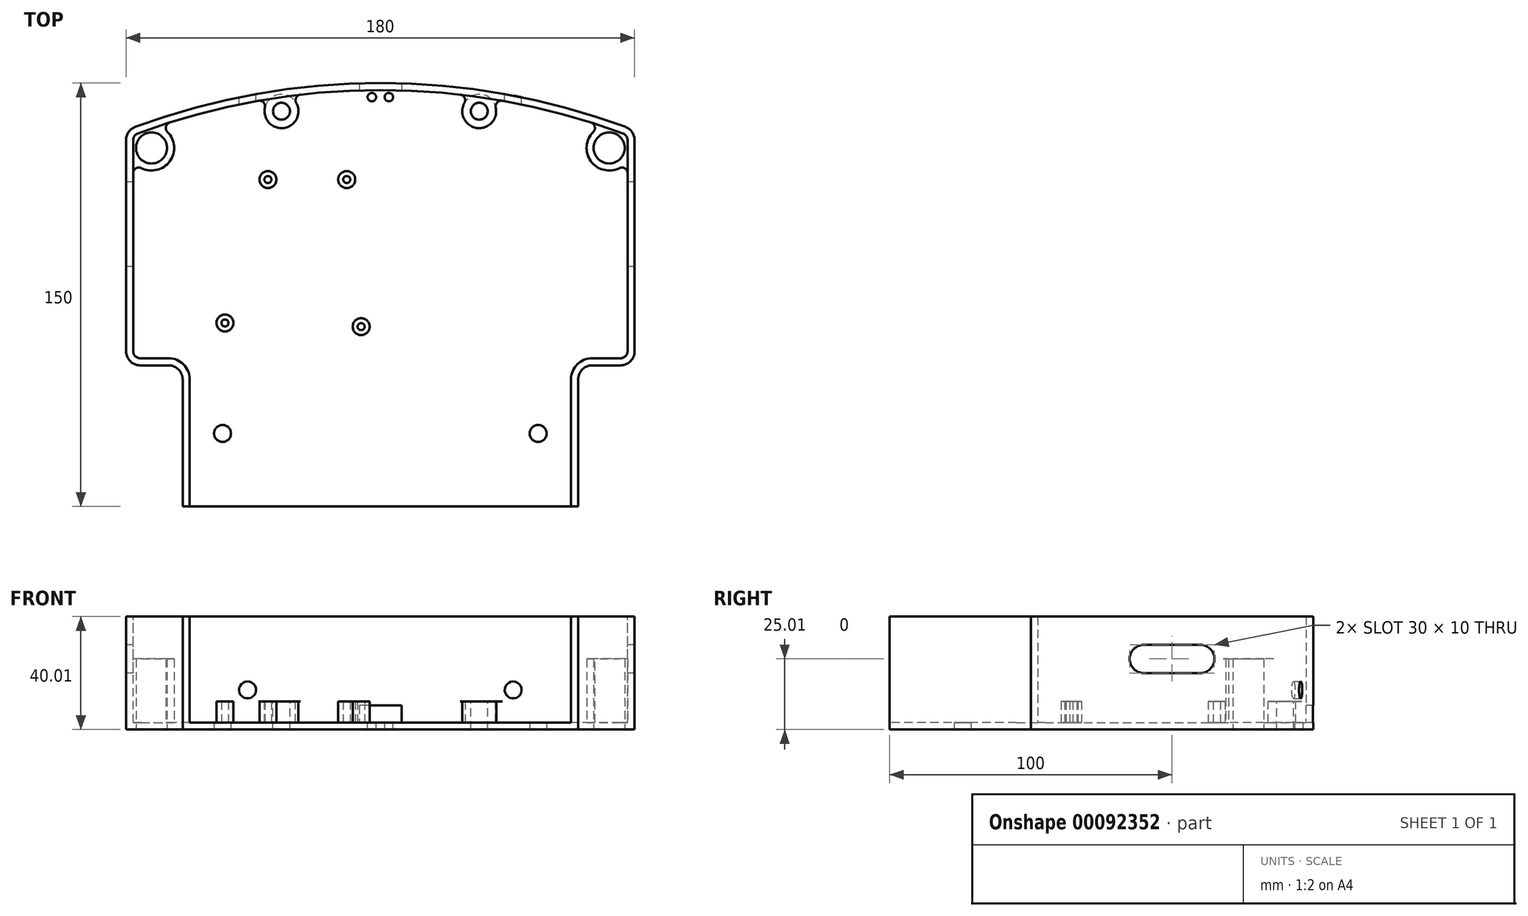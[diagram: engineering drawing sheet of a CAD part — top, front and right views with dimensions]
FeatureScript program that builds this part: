
annotation { "Feature Type Name" : "Feature", "Feature Type Description" : "" }
export const myFeature = defineFeature(function(context is Context, id is Id, definition is map)
    precondition{}
    {
        {
            var Q0;
            Q0=qCreatedBy(makeId("Top.planeOp"),FACE);
            var sketch = newSketch(context, id + "F0", { "sketchPlane" : qUnion([Q0])});
            skLineSegment(sketch, "E0.bottom", {"start": v(-90, -50) * mm, "end": v(90, -50) * mm});
            skLineSegment(sketch, "E0.top", {"start": v(-90, 100) * mm, "end": v(90, 100) * mm});
            skLineSegment(sketch, "E0.left", {"start": v(-90, -50) * mm, "end": v(-90, 100) * mm});
            skLineSegment(sketch, "E0.right", {"start": v(90, -50) * mm, "end": v(90, 100) * mm});
            skCircle(sketch, "E1", {"center": v(0, -150) * mm, "radius": 250 * mm});
            skSolve(sketch);
        }
        {
            var Q0;
            {var subQ4=sQuery(id+"F0.wireOp",EDGE,"E0.bottom");Q0=makeQuery(id+"F0.imprint","IMPRINT",FACE,{"disambiguationData":[TD([[makeQuery(id+"F0.imprint","IMPRINT",EDGE,{"derivedFrom":subQ4}),1.0]])]});}
            extrude(context, id + "F1", {"entities" : qUnion([Q0]), "depth" : 40 * mm});
        }
        {
            var Q0;
            Q0=qCreatedBy(makeId("Top.planeOp"),FACE);
            var sketch = newSketch(context, id + "F2", { "sketchPlane" : qUnion([Q0])});
            skLineSegment(sketch, "E2.bottom", {"start": v(-170, 0) * mm, "end": v(-70, 0) * mm});
            skLineSegment(sketch, "E2.top", {"start": v(-170, -200) * mm, "end": v(-70, -200) * mm});
            skLineSegment(sketch, "E2.left", {"start": v(-170, 0) * mm, "end": v(-170, -200) * mm});
            skLineSegment(sketch, "E2.right", {"start": v(-70, 0) * mm, "end": v(-70, -200) * mm});
            skLineSegment(sketch, "E3.bottom", {"start": v(170, 0) * mm, "end": v(70, 0) * mm});
            skLineSegment(sketch, "E3.top", {"start": v(170, -200) * mm, "end": v(70, -200) * mm});
            skLineSegment(sketch, "E3.left", {"start": v(170, 0) * mm, "end": v(170, -200) * mm});
            skLineSegment(sketch, "E3.right", {"start": v(70, 0) * mm, "end": v(70, -200) * mm});
            skSolve(sketch);
        }
        {
            var Q0;
            Q0=makeQuery(id+"F2.imprint","IMPRINT",FACE,{"disambiguationData":[TD([[makeQuery(id+"F2.imprint","IMPRINT",EDGE,{"derivedFrom":sQuery(id+"F2.wireOp",EDGE,"E2.bottom")}),-1.0]])]});
            var Q1;
            Q1=makeQuery(id+"F2.imprint","IMPRINT",FACE,{"disambiguationData":[TD([[makeQuery(id+"F2.imprint","IMPRINT",EDGE,{"derivedFrom":sQuery(id+"F2.wireOp",EDGE,"E3.bottom")}),1.0]])]});
            extrude(context, id + "F3", {"entities" : qUnion([Q0, Q1]), "operationType" : NewBodyOperationType.REMOVE, "depth" : 100 * mm});
        }
        {
            var Q0;
            Q0=makeQuery(id+"F1.opExtrude","SWEPT_EDGE",EDGE,{"disambiguationData":[OSD([sQuery(id+"F0.wireOp",EDGE,"E0.left"),sQuery(id+"F0.wireOp",EDGE,"E1")])]});
            var Q1;
            Q1=makeQuery(id+"F1.opExtrude","SWEPT_EDGE",EDGE,{"disambiguationData":[OSD([sQuery(id+"F0.wireOp",EDGE,"E0.right"),sQuery(id+"F0.wireOp",EDGE,"E1")])]});
            var Q2;
            Q2=makeQuery(id+"F3.boolean.opBoolean","INTERSECT",EDGE,{"derivedFrom":[makeQuery(id+"F1.opExtrude","SWEPT_FACE",FACE,{"disambiguationData":[OSD([sQuery(id+"F0.wireOp",EDGE,"E0.right")])]}),makeQuery(id+"F3.opExtrude","SWEPT_FACE",FACE,{"disambiguationData":[OSD([sQuery(id+"F2.wireOp",EDGE,"E3.bottom")])]})]});
            var Q3;
            Q3=makeQuery(id+"F3.boolean.opBoolean","COPY",EDGE,{"derivedFrom":makeQuery(id+"F3.opExtrude","SWEPT_EDGE",EDGE,{"disambiguationData":[OSD([sQuery(id+"F2.wireOp",EDGE,"E3.bottom"),sQuery(id+"F2.wireOp",EDGE,"E3.right")])]})});
            var Q4;
            Q4=makeQuery(id+"F3.boolean.opBoolean","INTERSECT",EDGE,{"derivedFrom":[makeQuery(id+"F1.opExtrude","SWEPT_FACE",FACE,{"disambiguationData":[OSD([sQuery(id+"F0.wireOp",EDGE,"E0.left")])]}),makeQuery(id+"F3.opExtrude","SWEPT_FACE",FACE,{"disambiguationData":[OSD([sQuery(id+"F2.wireOp",EDGE,"E2.bottom")])]})]});
            var Q5;
            Q5=makeQuery(id+"F3.boolean.opBoolean","COPY",EDGE,{"derivedFrom":makeQuery(id+"F3.opExtrude","SWEPT_EDGE",EDGE,{"disambiguationData":[OSD([sQuery(id+"F2.wireOp",EDGE,"E2.bottom"),sQuery(id+"F2.wireOp",EDGE,"E2.right")])]})});
            fillet(context, id + "F4", {"entities" : qUnion([Q0, Q1, Q2, Q3, Q4, Q5]), "radius" : 5 * mm, "tangentPropagation" : true, "allowEdgeOverflow" : false});
        }
        {
            var Q0;
            Q0=makeQuery(id+"F1.opExtrude","CAP_FACE",FACE,{"disambiguationData":[OSD([sQuery(id+"F0.wireOp",EDGE,"E0.bottom"),sQuery(id+"F0.wireOp",EDGE,"E0.left"),sQuery(id+"F0.wireOp",EDGE,"E0.right"),sQuery(id+"F0.wireOp",EDGE,"E1")])],"isStart":false});
            var Q1;
            Q1=makeQuery(id+"F1.opExtrude","SWEPT_FACE",FACE,{"disambiguationData":[OSD([sQuery(id+"F0.wireOp",EDGE,"E0.bottom")])]});
            shell(context, id + "F5", {"entities" : qUnion([Q0, Q1]), "thickness" : 2.5 * mm});
        }
        {
            var Q0;
            Q0=qCreatedBy(makeId("Top.planeOp"),FACE);
            var sketch = newSketch(context, id + "F6", { "sketchPlane" : qUnion([Q0])});
            skCircle(sketch, "E4", {"center": v(-55.86, -24.14) * mm, "radius": 3 * mm});
            skCircle(sketch, "E5", {"center": v(55.86, -24.14) * mm, "radius": 3 * mm});
            skLineSegment(sketch, "E6", {"start": v(0, -80) * mm, "end": v(-55.86, -24.14) * mm, "construction": true});
            skLineSegment(sketch, "E7", {"start": v(0, -80) * mm, "end": v(55.86, -24.14) * mm, "construction": true});
            skSolve(sketch);
        }
        {
            var Q0;
            Q0 = qSketchRegion(id + "F6", true);
            extrude(context, id + "F7", {"entities" : qUnion([Q0]), "operationType" : NewBodyOperationType.REMOVE, "depth" : 25 * mm});
        }
        {
            var Q0;
            Q0=qCreatedBy(makeId("Top.planeOp"),FACE);
            var sketch = newSketch(context, id + "F8", { "sketchPlane" : qUnion([Q0])});
            skCircle(sketch, "E8", {"center": v(-81, 77) * mm, "radius": 8 * mm});
            skCircle(sketch, "E9", {"center": v(81, 77) * mm, "radius": 8 * mm});
            skSolve(sketch);
        }
        {
            var Q0;
            Q0 = qSketchRegion(id + "F8", true);
            extrude(context, id + "F9", {"entities" : qUnion([Q0]), "operationType" : NewBodyOperationType.ADD, "depth" : 25 * mm});
        }
        {
            var Q0;
            Q0=qCreatedBy(makeId("Top.planeOp"),FACE);
            var sketch = newSketch(context, id + "F10", { "sketchPlane" : qUnion([Q0])});
            skCircle(sketch, "E10", {"center": v(-81, 77) * mm, "radius": 5.5 * mm});
            skCircle(sketch, "E11", {"center": v(81, 77) * mm, "radius": 5.5 * mm});
            skSolve(sketch);
        }
        {
            var Q0;
            Q0 = qSketchRegion(id + "F10", true);
            extrude(context, id + "F11", {"entities" : qUnion([Q0]), "operationType" : NewBodyOperationType.REMOVE, "depth" : 25 * mm});
        }
        {
            var Q0;
            Q0=qCreatedBy(makeId("Top.planeOp"),FACE);
            var sketch = newSketch(context, id + "F12", { "sketchPlane" : qUnion([Q0])});
            skCircle(sketch, "E12", {"center": v(-55, 15) * mm, "radius": 3 * mm});
            skCircle(sketch, "E13", {"center": v(-55, 15) * mm, "radius": 1.25 * mm});
            skCircle(sketch, "E14", {"center": v(-39.8, 65.8) * mm, "radius": 1.25 * mm});
            skCircle(sketch, "E15", {"center": v(-39.8, 65.8) * mm, "radius": 3 * mm});
            skCircle(sketch, "E16", {"center": v(-11.9, 65.8) * mm, "radius": 1.25 * mm});
            skCircle(sketch, "E17", {"center": v(-11.9, 65.8) * mm, "radius": 3 * mm});
            skCircle(sketch, "E18", {"center": v(-6.8, 13.7) * mm, "radius": 1.25 * mm});
            skCircle(sketch, "E19", {"center": v(-6.8, 13.7) * mm, "radius": 3 * mm});
            skSolve(sketch);
        }
        {
            var Q0;
            Q0 = qSketchRegion(id + "F12", true);
            extrude(context, id + "F13", {"entities" : qUnion([Q0]), "operationType" : NewBodyOperationType.ADD, "depth" : 10 * mm});
        }
        {
            var Q0;
            Q0=qCreatedBy(makeId("Front.planeOp"),FACE);
            var sketch = newSketch(context, id + "F14", { "sketchPlane" : qUnion([Q0])});
            skCircle(sketch, "E20", {"center": v(47, 14) * mm, "radius": 3 * mm});
            skCircle(sketch, "E21", {"center": v(-47, 14) * mm, "radius": 3 * mm});
            skSolve(sketch);
        }
        {
            var Q0;
            Q0 = qSketchRegion(id + "F14", true);
            extrude(context, id + "F15", {"entities" : qUnion([Q0]), "operationType" : NewBodyOperationType.REMOVE, "depth" : 300 * mm, "symmetric" : true});
        }
        {
            var Q0;
            Q0=qCreatedBy(makeId("Front.planeOp"),FACE);
            var sketch = newSketch(context, id + "F16", { "sketchPlane" : qUnion([Q0])});
            skLineSegment(sketch, "E22.bottom", {"start": v(7.5, 8.5) * mm, "end": v(-7.5, 8.5) * mm});
            skLineSegment(sketch, "E22.top", {"start": v(7.5, 2.5) * mm, "end": v(-7.5, 2.5) * mm});
            skLineSegment(sketch, "E22.left", {"start": v(7.5, 8.5) * mm, "end": v(7.5, 2.5) * mm});
            skLineSegment(sketch, "E22.right", {"start": v(-7.5, 8.5) * mm, "end": v(-7.5, 2.5) * mm});
            skSolve(sketch);
        }
        {
            var Q0;
            Q0=makeQuery(id+"F16.imprint","IMPRINT",FACE,{"disambiguationData":[TD([[makeQuery(id+"F16.imprint","IMPRINT",EDGE,{"derivedFrom":sQuery(id+"F16.wireOp",EDGE,"E22.bottom")}),1.0]])]});
            extrude(context, id + "F17", {"entities" : qUnion([Q0]), "operationType" : NewBodyOperationType.REMOVE, "oppositeDirection" : true, "depth" : 250 * mm, "hasSecondDirection" : true, "secondDirectionOppositeDirection" : true, "secondDirectionDepth" : 41.95 * mm});
        }
        {
            var Q0;
            Q0=qCreatedBy(makeId("Top.planeOp"),FACE);
            var sketch = newSketch(context, id + "F18", { "sketchPlane" : qUnion([Q0])});
            skCircle(sketch, "E23", {"center": v(3, 95) * mm, "radius": 1.5 * mm});
            skCircle(sketch, "E24", {"center": v(-3, 95) * mm, "radius": 1.5 * mm});
            skSolve(sketch);
        }
        {
            var Q0;
            Q0=makeQuery(id+"F18.imprint","IMPRINT",FACE,{"disambiguationData":[TD([[makeQuery(id+"F18.imprint","IMPRINT",EDGE,{"derivedFrom":sQuery(id+"F18.wireOp",EDGE,"E24")}),1.0]])]});
            var Q1;
            Q1=makeQuery(id+"F18.imprint","IMPRINT",FACE,{"disambiguationData":[TD([[makeQuery(id+"F18.imprint","IMPRINT",EDGE,{"derivedFrom":sQuery(id+"F18.wireOp",EDGE,"E23")}),1.0]])]});
            extrude(context, id + "F19", {"entities" : qUnion([Q0, Q1]), "operationType" : NewBodyOperationType.REMOVE, "oppositeDirection" : true, "depth" : 25 * mm, "symmetric" : true});
        }
        {
            var Q0;
            Q0=qCreatedBy(makeId("Top.planeOp"),FACE);
            var sketch = newSketch(context, id + "F20", { "sketchPlane" : qUnion([Q0])});
            skCircle(sketch, "E25", {"center": v(-35, 90) * mm, "radius": 6 * mm});
            skCircle(sketch, "E26", {"center": v(35, 90) * mm, "radius": 6 * mm});
            skSolve(sketch);
        }
        {
            var Q0;
            Q0 = qSketchRegion(id + "F20", true);
            extrude(context, id + "F21", {"entities" : qUnion([Q0]), "operationType" : NewBodyOperationType.ADD, "oppositeDirection" : true, "depth" : 0.01 * mm, "hasSecondDirection" : true, "secondDirectionOppositeDirection" : false, "secondDirectionDepth" : 10 * mm});
        }
        {
            var Q0;
            Q0=makeQuery(id+"F1.opExtrude","CAP_FACE",FACE,{"disambiguationData":[OSD([sQuery(id+"F0.wireOp",EDGE,"E0.bottom"),sQuery(id+"F0.wireOp",EDGE,"E0.left"),sQuery(id+"F0.wireOp",EDGE,"E0.right"),sQuery(id+"F0.wireOp",EDGE,"E1")])],"isStart":true});
            var sketch = newSketch(context, id + "F22", { "sketchPlane" : qUnion([Q0])});
            skCircle(sketch, "E27", {"center": v(-35, -90) * mm, "radius": 3 * mm});
            skCircle(sketch, "E28", {"center": v(35, -90) * mm, "radius": 3 * mm});
            skSolve(sketch);
        }
        {
            var Q0;
            Q0 = qSketchRegion(id + "F22", true);
            extrude(context, id + "F23", {"entities" : qUnion([Q0]), "operationType" : NewBodyOperationType.REMOVE, "depth" : 25 * mm, "symmetric" : true});
        }
        {
            var Q0;
            Q0=makeQuery(id+"F9.boolean.opBoolean","INTERSECT",EDGE,{"derivedFrom":[makeQuery(id+"F5.opShell","OFFSET_FACE",FACE,{"disambiguationData":[OSD([sQuery(id+"F0.wireOp",EDGE,"E0.left")])]}),makeQuery(id+"F9.opExtrude","SWEPT_FACE",FACE,{"disambiguationData":[OSD([sQuery(id+"F8.wireOp",EDGE,"E8")])]})]});
            var Q1;
            Q1=makeQuery(id+"F9.boolean.opBoolean","INTERSECT",EDGE,{"derivedFrom":[makeQuery(id+"F5.opShell","OFFSET_FACE",FACE,{"disambiguationData":[OSD([sQuery(id+"F0.wireOp",EDGE,"E1")])]}),makeQuery(id+"F9.opExtrude","SWEPT_FACE",FACE,{"disambiguationData":[OSD([sQuery(id+"F8.wireOp",EDGE,"E8")])]})]});
            var Q2;
            Q2=makeQuery(id+"F21.boolean.opBoolean","INTERSECT",EDGE,{"disambiguationData":[OD(0.0)],"derivedFrom":[makeQuery(id+"F5.opShell","OFFSET_FACE",FACE,{"disambiguationData":[OSD([sQuery(id+"F0.wireOp",EDGE,"E1")])]}),makeQuery(id+"F21.opExtrude","SWEPT_FACE",FACE,{"disambiguationData":[OSD([sQuery(id+"F20.wireOp",EDGE,"E25")])]})]});
            var Q3;
            Q3=makeQuery(id+"F21.boolean.opBoolean","INTERSECT",EDGE,{"disambiguationData":[OD(1.0)],"derivedFrom":[makeQuery(id+"F5.opShell","OFFSET_FACE",FACE,{"disambiguationData":[OSD([sQuery(id+"F0.wireOp",EDGE,"E1")])]}),makeQuery(id+"F21.opExtrude","SWEPT_FACE",FACE,{"disambiguationData":[OSD([sQuery(id+"F20.wireOp",EDGE,"E25")])]})]});
            var Q4;
            Q4=makeQuery(id+"F21.boolean.opBoolean","INTERSECT",EDGE,{"disambiguationData":[OD(1.0)],"derivedFrom":[makeQuery(id+"F5.opShell","OFFSET_FACE",FACE,{"disambiguationData":[OSD([sQuery(id+"F0.wireOp",EDGE,"E1")])]}),makeQuery(id+"F21.opExtrude","SWEPT_FACE",FACE,{"disambiguationData":[OSD([sQuery(id+"F20.wireOp",EDGE,"E26")])]})]});
            var Q5;
            Q5=makeQuery(id+"F21.boolean.opBoolean","INTERSECT",EDGE,{"disambiguationData":[OD(0.0)],"derivedFrom":[makeQuery(id+"F5.opShell","OFFSET_FACE",FACE,{"disambiguationData":[OSD([sQuery(id+"F0.wireOp",EDGE,"E1")])]}),makeQuery(id+"F21.opExtrude","SWEPT_FACE",FACE,{"disambiguationData":[OSD([sQuery(id+"F20.wireOp",EDGE,"E26")])]})]});
            var Q6;
            Q6=makeQuery(id+"F9.boolean.opBoolean","INTERSECT",EDGE,{"derivedFrom":[makeQuery(id+"F5.opShell","OFFSET_FACE",FACE,{"disambiguationData":[OSD([sQuery(id+"F0.wireOp",EDGE,"E1")])]}),makeQuery(id+"F9.opExtrude","SWEPT_FACE",FACE,{"disambiguationData":[OSD([sQuery(id+"F8.wireOp",EDGE,"E9")])]})]});
            var Q7;
            Q7=makeQuery(id+"F9.boolean.opBoolean","INTERSECT",EDGE,{"derivedFrom":[makeQuery(id+"F5.opShell","OFFSET_FACE",FACE,{"disambiguationData":[OSD([sQuery(id+"F0.wireOp",EDGE,"E0.right")])]}),makeQuery(id+"F9.opExtrude","SWEPT_FACE",FACE,{"disambiguationData":[OSD([sQuery(id+"F8.wireOp",EDGE,"E9")])]})]});
            fillet(context, id + "F24", {"entities" : qUnion([Q0, Q1, Q2, Q3, Q4, Q5, Q6, Q7]), "radius" : 2 * mm, "tangentPropagation" : true, "allowEdgeOverflow" : false});
        }
        {
            var Q0;
            Q0=qCreatedBy(makeId("Right.planeOp"),FACE);
            var sketch = newSketch(context, id + "F25", { "sketchPlane" : qUnion([Q0])});
            skLineSegment(sketch, "E29.bottom", {"start": v(40, 30) * mm, "end": v(60, 30) * mm});
            skLineSegment(sketch, "E29.top", {"start": v(40, 20) * mm, "end": v(60, 20) * mm});
            skLineSegment(sketch, "E29.left", {"start": v(40, 30) * mm, "end": v(40, 20) * mm});
            skLineSegment(sketch, "E29.right", {"start": v(60, 30) * mm, "end": v(60, 20) * mm});
            skCircle(sketch, "E30", {"center": v(40, 25) * mm, "radius": 5 * mm});
            skCircle(sketch, "E31", {"center": v(60, 25) * mm, "radius": 5 * mm});
            skSolve(sketch);
        }
        {
            var Q0;
            {var subQ0=sQuery(id+"F25.wireOp",EDGE,"E29.left");Q0=makeQuery(id+"F25.imprint","IMPRINT",FACE,{"disambiguationData":[TD([[makeQuery(id+"F25.imprint","IMPRINT",EDGE,{"derivedFrom":subQ0}),-1.0]])]});}
            var Q1;
            {var subQ0=sQuery(id+"F25.wireOp",EDGE,"E29.right");Q1=makeQuery(id+"F25.imprint","IMPRINT",FACE,{"disambiguationData":[TD([[makeQuery(id+"F25.imprint","IMPRINT",EDGE,{"derivedFrom":subQ0}),1.0]])]});}
            var Q2;
            {var subQ0=sQuery(id+"F25.wireOp",EDGE,"E29.bottom");Q2=makeQuery(id+"F25.imprint","IMPRINT",FACE,{"disambiguationData":[TD([[makeQuery(id+"F25.imprint","IMPRINT",EDGE,{"derivedFrom":subQ0}),-1.0]])]});}
            var Q3;
            {var subQ0=sQuery(id+"F25.wireOp",EDGE,"E29.left");Q3=makeQuery(id+"F25.imprint","IMPRINT",FACE,{"disambiguationData":[TD([[makeQuery(id+"F25.imprint","IMPRINT",EDGE,{"derivedFrom":subQ0}),1.0]])]});}
            var Q4;
            {var subQ0=sQuery(id+"F25.wireOp",EDGE,"E29.right");Q4=makeQuery(id+"F25.imprint","IMPRINT",FACE,{"disambiguationData":[TD([[makeQuery(id+"F25.imprint","IMPRINT",EDGE,{"derivedFrom":subQ0}),-1.0]])]});}
            extrude(context, id + "F26", {"entities" : qUnion([Q0, Q1, Q2, Q3, Q4]), "operationType" : NewBodyOperationType.REMOVE, "depth" : 300 * mm, "symmetric" : true});
        }
    });
